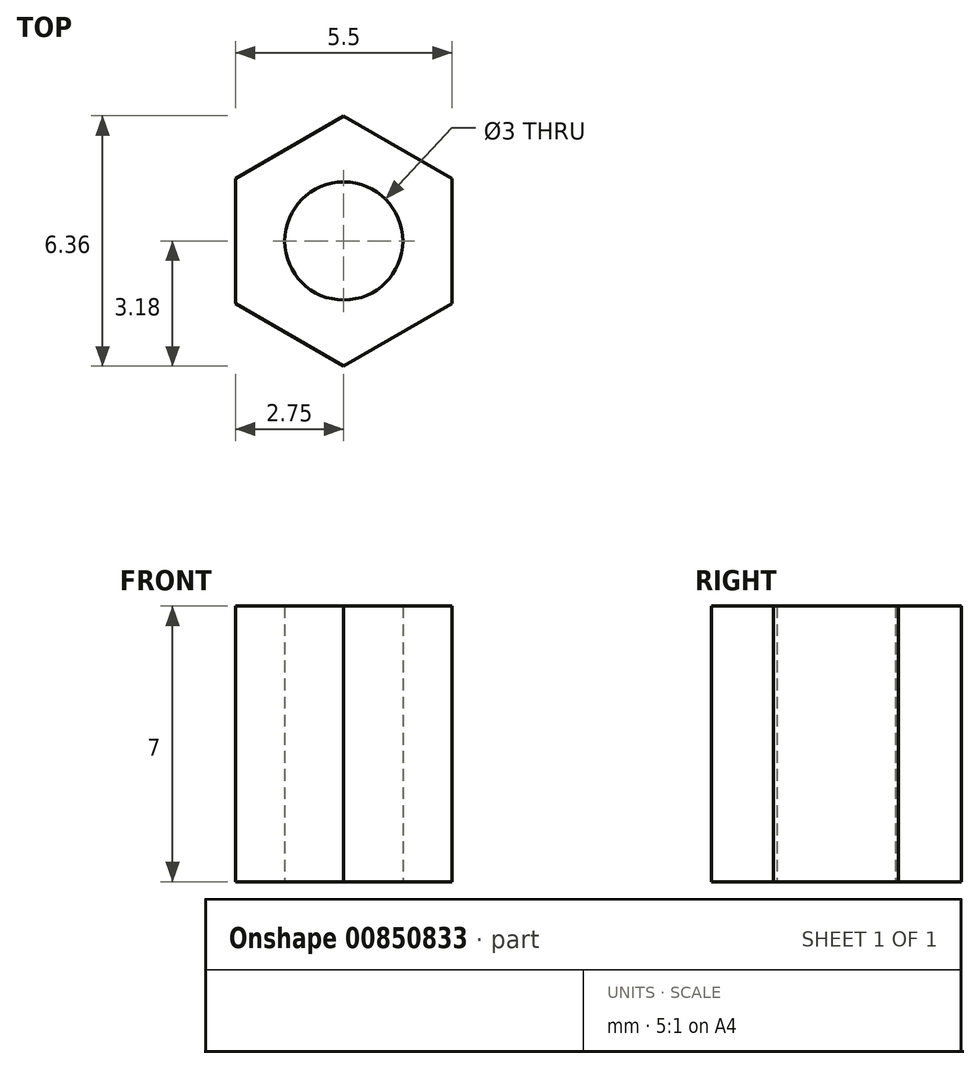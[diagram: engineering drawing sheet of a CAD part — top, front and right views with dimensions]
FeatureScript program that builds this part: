
annotation { "Feature Type Name" : "Feature", "Feature Type Description" : "" }
export const myFeature = defineFeature(function(context is Context, id is Id, definition is map)
    precondition{}
    {
        {
            var Q0;
            Q0=qCreatedBy(makeId("Top.planeOp"),FACE);
            var sketch = newSketch(context, id + "F0", { "sketchPlane" : qUnion([Q0])});
            skCircle(sketch, "E0.cCircle", {"center": v(0, 0) * mm, "radius": 3.18 * mm, "construction": true});
            skLineSegment(sketch, "E0.0", {"start": v(2.75, 1.59) * mm, "end": v(2.75, -1.59) * mm});
            skLineSegment(sketch, "E0.1", {"start": v(2.75, -1.59) * mm, "end": v(0, -3.18) * mm});
            skLineSegment(sketch, "E0.2", {"start": v(0, -3.18) * mm, "end": v(-2.75, -1.59) * mm});
            skLineSegment(sketch, "E0.3", {"start": v(-2.75, -1.59) * mm, "end": v(-2.75, 1.59) * mm});
            skLineSegment(sketch, "E0.4", {"start": v(-2.75, 1.59) * mm, "end": v(0, 3.18) * mm});
            skLineSegment(sketch, "E0.5", {"start": v(0, 3.18) * mm, "end": v(2.75, 1.59) * mm});
            skCircle(sketch, "E1", {"center": v(0, 0) * mm, "radius": 1.5 * mm});
            skSolve(sketch);
        }
        {
            var Q0;
            Q0=qSketchRegion(id+"F0",true);
            extrude(context, id + "F1", {"entities" : qUnion([Q0]), "depth" : 7 * mm, "offsetDistance" : 25 * mm});
        }
        {
            var Q0;
            Q0=makeQuery(id+"F0.imprint","IMPRINT",FACE,{"disambiguationData":[TD([[makeQuery(id+"F0.imprint","IMPRINT",EDGE,{"derivedFrom":sQuery(id+"F0.wireOp",EDGE,"E1")}),1.0]])]});
            extrude(context, id + "F2", {"entities" : qUnion([Q0]), "operationType" : NewBodyOperationType.REMOVE, "depth" : 5 * mm, "offsetDistance" : 25 * mm});
        }
    });
